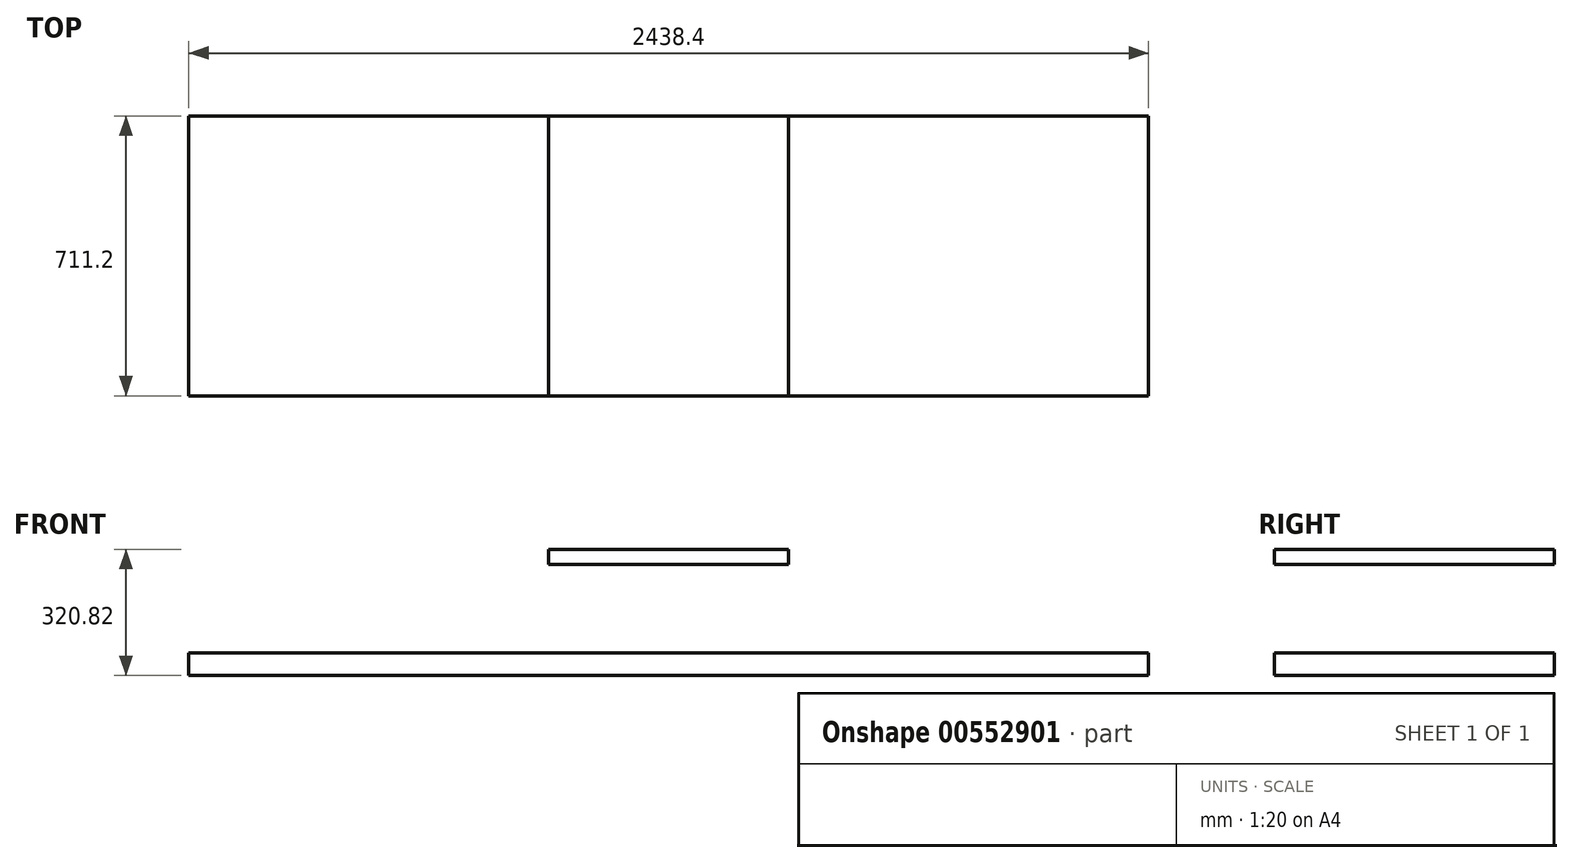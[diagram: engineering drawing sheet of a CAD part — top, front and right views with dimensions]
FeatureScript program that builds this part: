
annotation { "Feature Type Name" : "Feature", "Feature Type Description" : "" }
export const myFeature = defineFeature(function(context is Context, id is Id, definition is map)
    precondition{}
    {
        {
            var Q0;
            Q0=qCreatedBy(makeId("Right.planeOp"),FACE);
            var sketch = newSketch(context, id + "F0", { "sketchPlane" : qUnion([Q0])});
            skLineSegment(sketch, "E0.bottom", {"start": v(355.6, -28.57) * mm, "end": v(-355.6, -28.58) * mm});
            skLineSegment(sketch, "E0.top", {"start": v(355.6, 28.58) * mm, "end": v(-355.6, 28.57) * mm});
            skLineSegment(sketch, "E0.left", {"start": v(355.6, -28.57) * mm, "end": v(355.6, 28.58) * mm});
            skLineSegment(sketch, "E0.right", {"start": v(-355.6, -28.58) * mm, "end": v(-355.6, 28.57) * mm});
            skPoint(sketch, "E0.middle", {"position": v(0, 0) * mm});
            skSolve(sketch);
        }
        {
            var Q0;
            Q0 = qSketchRegion(id + "F0", true);
            extrude(context, id + "F1", {"entities" : qUnion([Q0]), "endBound" : BoundingType.SYMMETRIC, "depth" : 2438.4 * mm, "offsetDistance" : 25.4 * mm});
        }
        {
            var Q0;
            Q0=qCreatedBy(makeId("Right.planeOp"),FACE);
            var sketch = newSketch(context, id + "F2", { "sketchPlane" : qUnion([Q0])});
            skLineSegment(sketch, "E1.bottom", {"start": v(355.6, 292.25) * mm, "end": v(-355.6, 292.25) * mm});
            skLineSegment(sketch, "E1.top", {"start": v(355.6, 254.15) * mm, "end": v(-355.6, 254.15) * mm});
            skLineSegment(sketch, "E1.left", {"start": v(355.6, 292.25) * mm, "end": v(355.6, 254.15) * mm});
            skLineSegment(sketch, "E1.right", {"start": v(-355.6, 292.25) * mm, "end": v(-355.6, 254.15) * mm});
            skPoint(sketch, "E1.middle", {"position": v(0, 273.2) * mm});
            skSolve(sketch);
        }
        {
            var Q0;
            Q0 = qSketchRegion(id + "F2", true);
            extrude(context, id + "F3", {"entities" : qUnion([Q0]), "endBound" : BoundingType.SYMMETRIC, "depth" : 609.6 * mm, "offsetDistance" : 25.4 * mm});
        }
    });
